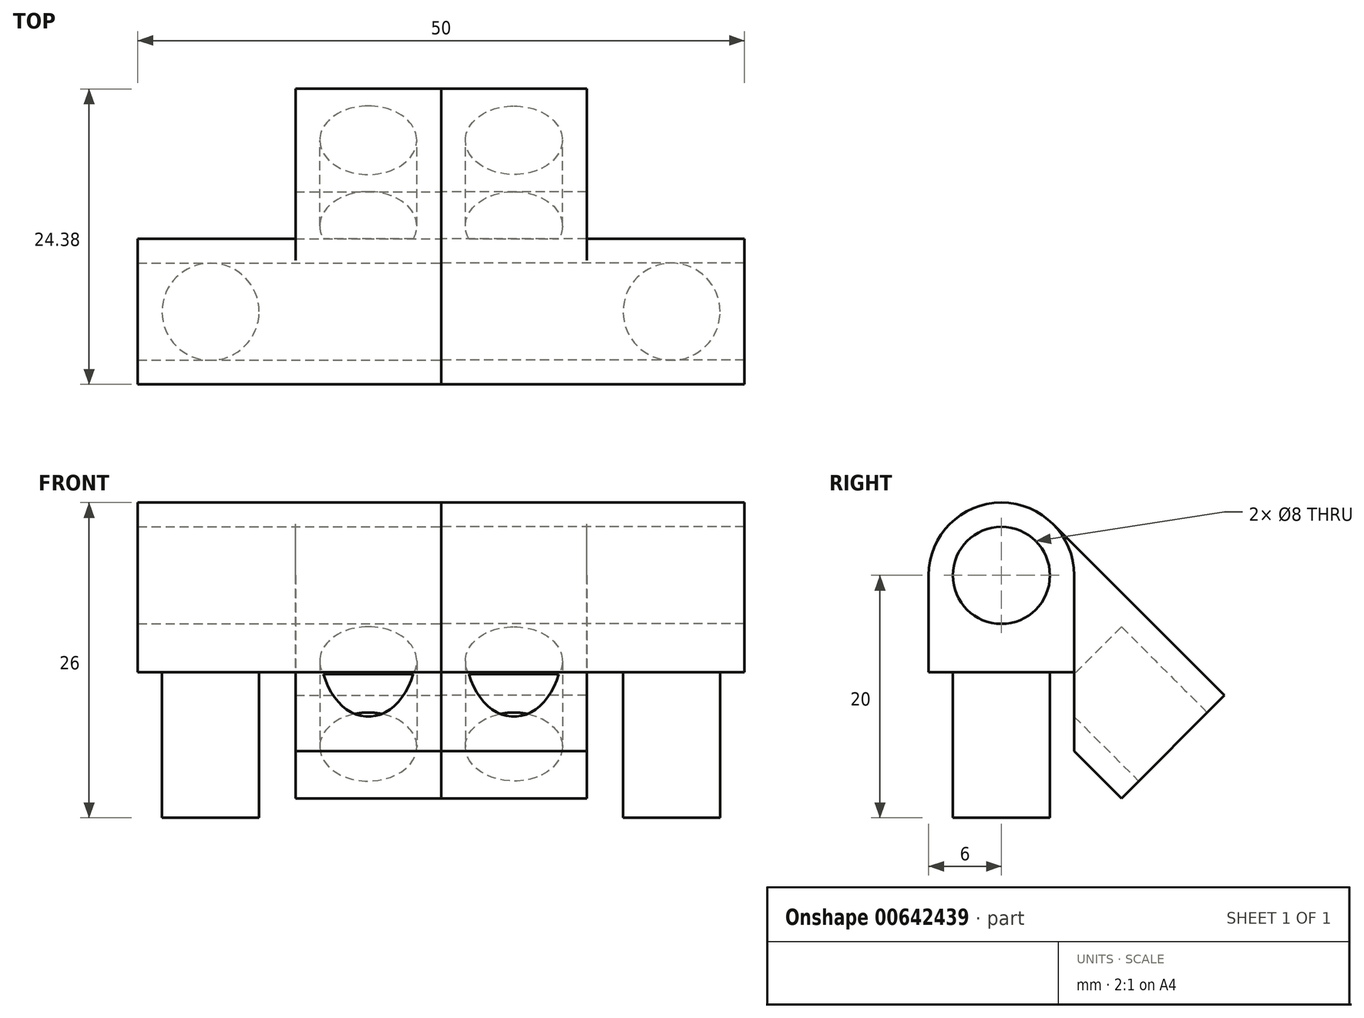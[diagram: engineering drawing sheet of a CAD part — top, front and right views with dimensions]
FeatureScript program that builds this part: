
annotation { "Feature Type Name" : "Feature", "Feature Type Description" : "" }
export const myFeature = defineFeature(function(context is Context, id is Id, definition is map)
    precondition{}
    {
        {
            var Q0;
            Q0=qCreatedBy(makeId("Right.planeOp"),FACE);
            var sketch = newSketch(context, id + "F0", { "sketchPlane" : qUnion([Q0])});
            skCircle(sketch, "E0", {"center": v(0, 0) * mm, "radius": 4 * mm});
            skCircle(sketch, "E1", {"center": v(0, 0) * mm, "radius": 6 * mm});
            skLineSegment(sketch, "E2", {"start": v(-6, 0) * mm, "end": v(-6, -20) * mm});
            skLineSegment(sketch, "E3", {"start": v(6, 0) * mm, "end": v(6, -20) * mm});
            skLineSegment(sketch, "E4", {"start": v(-6, -20) * mm, "end": v(6, -20) * mm});
            skLineSegment(sketch, "E5", {"start": v(0, 0) * mm, "end": v(13.82, -13.82) * mm, "construction": true});
            skLineSegment(sketch, "E6.MirrorCS", {"start": v(-4.24, -4.24) * mm, "end": v(9.9, -18.38) * mm});
            skLineSegment(sketch, "E7", {"start": v(18.38, -9.9) * mm, "end": v(4.24, 4.24) * mm});
            skLineSegment(sketch, "E8", {"start": v(18.38, -9.9) * mm, "end": v(9.9, -18.38) * mm});
            skSolve(sketch);
        }
        {
            var Q0;
            {var subQ4=sQuery(id+"F0.wireOp",EDGE,"E2");Q0=makeQuery(id+"F0.imprint","IMPRINT",FACE,{"disambiguationData":[TD([[makeQuery(id+"F0.imprint","IMPRINT",EDGE,{"derivedFrom":subQ4}),1.0]])]});}
            var Q1;
            {var subQ0=sQuery(id+"F0.wireOp",EDGE,"E3");var subQ1=sQuery(id+"F0.wireOp",EDGE,"E1");var subQ2=makeQuery(id+"F0.imprint","INTERSECT",VERTEX,{"derivedFrom":[subQ1,subQ0]});Q1=makeQuery(id+"F0.imprint","IMPRINT",FACE,{"disambiguationData":[TD([[makeQuery(id+"F0.imprint","IMPRINT",EDGE,{"disambiguationData":[TD([[subQ2,1.0]])],"derivedFrom":subQ1}),-1.0]])]});}
            var Q2;
            Q2=makeQuery(id+"F0.imprint","IMPRINT",FACE,{"disambiguationData":[TD([[makeQuery(id+"F0.imprint","IMPRINT",EDGE,{"derivedFrom":sQuery(id+"F0.wireOp",EDGE,"E0")}),-1.0]])]});
            extrude(context, id + "F1", {"entities" : qUnion([Q0, Q1, Q2]), "depth" : 25 * mm, "offsetDistance" : 25 * mm});
        }
        {
            var Q0;
            {var subQ4=sQuery(id+"F0.wireOp",EDGE,"E7");Q0=makeQuery(id+"F0.imprint","IMPRINT",FACE,{"disambiguationData":[TD([[makeQuery(id+"F0.imprint","IMPRINT",EDGE,{"derivedFrom":subQ4}),1.0]])]});}
            extrude(context, id + "F2", {"entities" : qUnion([Q0]), "operationType" : NewBodyOperationType.ADD, "depth" : 12 * mm, "offsetDistance" : 25 * mm});
        }
        {
            var Q0;
            Q0=makeQuery(id+"F1.opExtrude","SWEPT_FACE",FACE,{"disambiguationData":[OSD([sQuery(id+"F0.wireOp",EDGE,"E4")])]});
            var sketch = newSketch(context, id + "F3", { "sketchPlane" : qUnion([Q0])});
            skLineSegment(sketch, "E9", {"start": v(12.5, 6) * mm, "end": v(12.5, -6) * mm, "construction": true});
            skCircle(sketch, "E10", {"center": v(6, 0) * mm, "radius": 4 * mm});
            skCircle(sketch, "E11.MirrorC", {"center": v(19, 0) * mm, "radius": 4 * mm});
            skSolve(sketch);
        }
        {
            var Q0;
            Q0=makeQuery(id+"F3.imprint","IMPRINT",FACE,{"disambiguationData":[TD([[makeQuery(id+"F3.imprint","IMPRINT",EDGE,{"derivedFrom":sQuery(id+"F3.wireOp",EDGE,"E11.MirrorC")}),-1.0]])]});
            var Q1;
            Q1=makeQuery(id+"F3.imprint","IMPRINT",FACE,{"disambiguationData":[TD([[makeQuery(id+"F3.imprint","IMPRINT",EDGE,{"derivedFrom":sQuery(id+"F3.wireOp",EDGE,"E10")}),1.0]])]});
            extrude(context, id + "F4", {"entities" : qUnion([Q0, Q1]), "operationType" : NewBodyOperationType.REMOVE, "oppositeDirection" : true, "depth" : 12 * mm, "offsetDistance" : 25 * mm});
        }
        {
            var Q0;
            Q0=makeQuery(id+"F2.opExtrude","SWEPT_FACE",FACE,{"disambiguationData":[OSD([sQuery(id+"F0.wireOp",EDGE,"E8")])]});
            var sketch = newSketch(context, id + "F5", { "sketchPlane" : qUnion([Q0])});
            skCircle(sketch, "E12", {"center": v(-6, 0) * mm, "radius": 4 * mm});
            skSolve(sketch);
        }
        {
            var Q0;
            Q0=makeQuery(id+"F5.imprint","IMPRINT",FACE,{"disambiguationData":[TD([[makeQuery(id+"F5.imprint","IMPRINT",EDGE,{"derivedFrom":sQuery(id+"F5.wireOp",EDGE,"E12")}),1.0]])]});
            extrude(context, id + "F6", {"entities" : qUnion([Q0]), "operationType" : NewBodyOperationType.REMOVE, "oppositeDirection" : true, "depth" : 10 * mm, "offsetDistance" : 25 * mm});
        }
        {
            var Q0;
            Q0=makeQuery(id+"F1.opExtrude","SWEPT_BODY",BODY,{"disambiguationData":[OSD([sQuery(id+"F0.wireOp",EDGE,"E0"),sQuery(id+"F0.wireOp",EDGE,"E1"),sQuery(id+"F0.wireOp",EDGE,"E2"),sQuery(id+"F0.wireOp",EDGE,"E3"),sQuery(id+"F0.wireOp",EDGE,"E4")])]});
            var Q1;
            Q1=qCreatedBy(makeId("Right.planeOp"),FACE);
            mirror(context, id + "F7", {"entities" : qUnion([Q0]), "mirrorPlane" : qUnion([Q1])});
        }
    });
